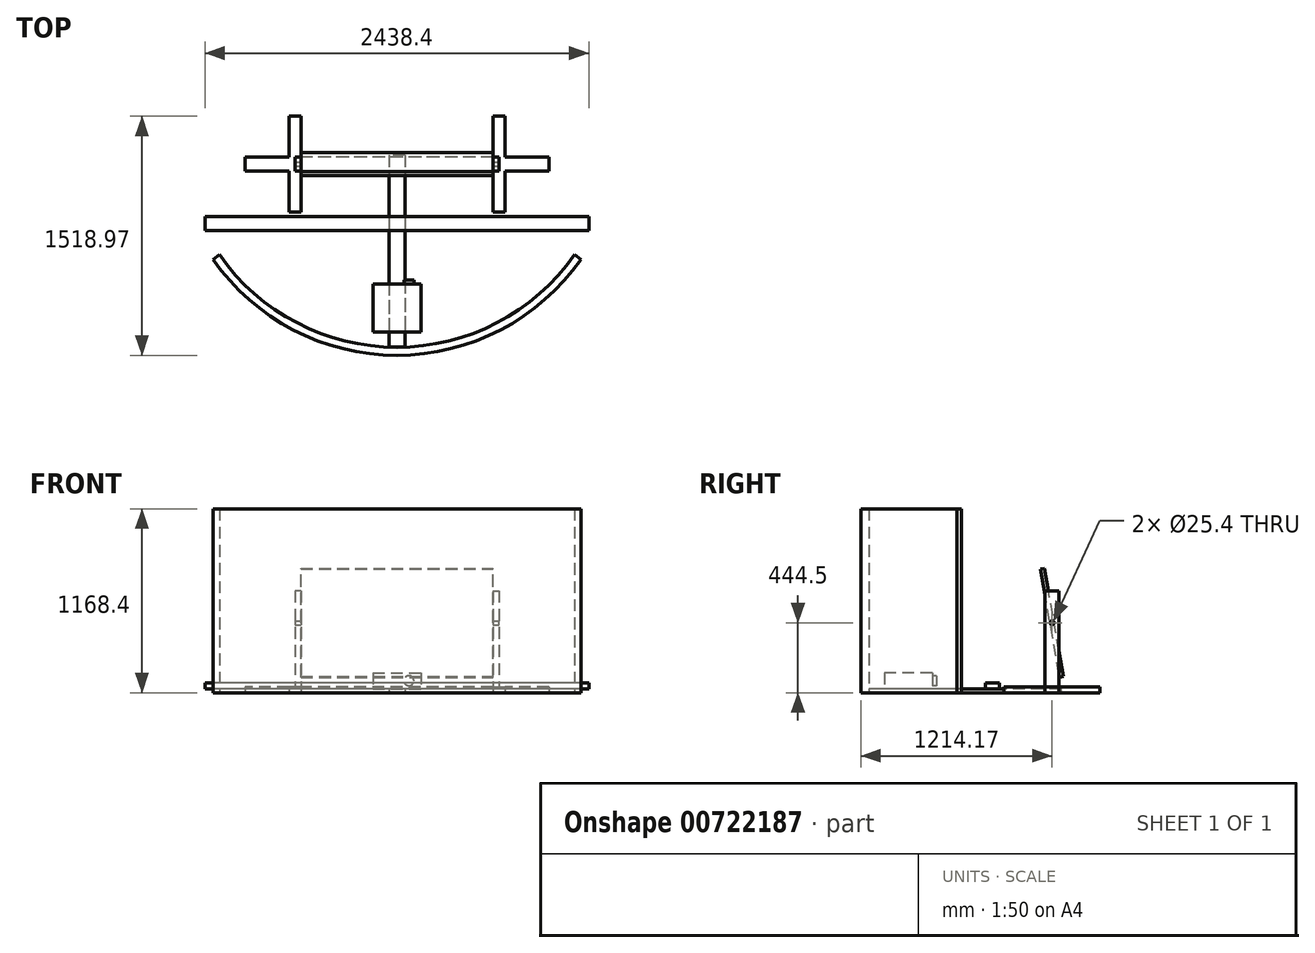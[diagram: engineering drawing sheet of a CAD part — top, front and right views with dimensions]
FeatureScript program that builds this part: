
annotation { "Feature Type Name" : "Feature", "Feature Type Description" : "" }
export const myFeature = defineFeature(function(context is Context, id is Id, definition is map)
    precondition{}
    {
        {
            var Q0;
            Q0=qCreatedBy(makeId("Top.planeOp"),FACE);
            var sketch = newSketch(context, id + "F0", { "sketchPlane" : qUnion([Q0])});
            skArc(sketch, "E0", {"start": v(-1168.4, -203.2) * mm, "mid": v(0, -812.8) * mm, "end": v(1168.4, -203.2) * mm});
            skLineSegment(sketch, "E1", {"start": v(0, 0) * mm, "end": v(0, -812.8) * mm, "construction": true});
            skPoint(sketch, "E2", {"position": v(0, -812.8) * mm});
            skArc(sketch, "E3.0", {"start": v(-1126.73, -174.14) * mm, "mid": v(0, -762) * mm, "end": v(1126.73, -174.14) * mm});
            skLineSegment(sketch, "E4", {"start": v(-1168.4, -203.2) * mm, "end": v(-1126.73, -174.14) * mm});
            skLineSegment(sketch, "E5", {"start": v(-1182.16, -183.48) * mm, "end": v(-1140.04, -243.86) * mm, "construction": true});
            skLineSegment(sketch, "E6.MirrorCS", {"start": v(1168.4, -203.2) * mm, "end": v(1126.73, -174.14) * mm});
            skSolve(sketch);
        }
        {
            var Q0;
            Q0 = qSketchRegion(id + "F0", true);
            extrude(context, id + "F1", {"entities" : qUnion([Q0]), "depth" : 1168.4 * mm, "offsetDistance" : 25.4 * mm});
        }
        {
            var Q0;
            Q0=qCreatedBy(makeId("Top.planeOp"),FACE);
            var sketch = newSketch(context, id + "F2", { "sketchPlane" : qUnion([Q0])});
            skLineSegment(sketch, "E7.bottom", {"start": v(50.8, 458.14) * mm, "end": v(-50.8, 458.14) * mm});
            skLineSegment(sketch, "E7.top", {"start": v(50.8, -761.06) * mm, "end": v(-50.8, -761.06) * mm});
            skLineSegment(sketch, "E7.left", {"start": v(50.8, 458.14) * mm, "end": v(50.8, -761.06) * mm});
            skLineSegment(sketch, "E7.right", {"start": v(-50.8, 458.14) * mm, "end": v(-50.8, -761.06) * mm});
            skPoint(sketch, "E7.middle", {"position": v(0, -151.46) * mm});
            skSolve(sketch);
        }
        {
            var Q0;
            Q0 = qSketchRegion(id + "F2", true);
            extrude(context, id + "F3", {"entities" : qUnion([Q0]), "depth" : 25.4 * mm, "offsetDistance" : 25.4 * mm});
        }
        {
            var Q0;
            Q0=makeQuery(id+"F3.opExtrude","CAP_FACE",FACE,{"disambiguationData":[OSD([sQuery(id+"F2.wireOp",EDGE,"E7.bottom"),sQuery(id+"F2.wireOp",EDGE,"E7.top"),sQuery(id+"F2.wireOp",EDGE,"E7.left"),sQuery(id+"F2.wireOp",EDGE,"E7.right")])],"isStart":false});
            var sketch = newSketch(context, id + "F4", { "sketchPlane" : qUnion([Q0])});
            skLineSegment(sketch, "E8.bottom", {"start": v(-152.4, -359.61) * mm, "end": v(152.4, -359.61) * mm});
            skLineSegment(sketch, "E8.top", {"start": v(-152.4, -664.41) * mm, "end": v(152.4, -664.41) * mm});
            skLineSegment(sketch, "E8.left", {"start": v(-152.4, -359.61) * mm, "end": v(-152.4, -664.41) * mm});
            skLineSegment(sketch, "E8.right", {"start": v(152.4, -359.61) * mm, "end": v(152.4, -664.41) * mm});
            skPoint(sketch, "E8.middle", {"position": v(0, -512.01) * mm});
            skSolve(sketch);
        }
        {
            var Q0;
            Q0 = qSketchRegion(id + "F4", true);
            extrude(context, id + "F5", {"entities" : qUnion([Q0]), "depth" : 101.6 * mm, "offsetDistance" : 25.4 * mm});
        }
        {
            var Q0;
            Q0=makeQuery(id+"F5.opExtrude","SWEPT_FACE",FACE,{"disambiguationData":[OSD([sQuery(id+"F4.wireOp",EDGE,"E8.bottom")])]});
            var sketch = newSketch(context, id + "F6", { "sketchPlane" : qUnion([Q0])});
            skCircle(sketch, "E9", {"center": v(-76.2, 76.2) * mm, "radius": 31.75 * mm});
            skLineSegment(sketch, "E10", {"start": v(-152.4, 76.2) * mm, "end": v(-13.38, 76.2) * mm, "construction": true});
            skSolve(sketch);
        }
        {
            var Q0;
            Q0 = qSketchRegion(id + "F6", true);
            extrude(context, id + "F7", {"entities" : qUnion([Q0]), "operationType" : NewBodyOperationType.ADD, "depth" : 25.4 * mm, "offsetDistance" : 25.4 * mm});
        }
        {
            var Q0;
            Q0=makeQuery(id+"F3.opExtrude","CAP_FACE",FACE,{"disambiguationData":[OSD([sQuery(id+"F2.wireOp",EDGE,"E7.bottom"),sQuery(id+"F2.wireOp",EDGE,"E7.top"),sQuery(id+"F2.wireOp",EDGE,"E7.left"),sQuery(id+"F2.wireOp",EDGE,"E7.right")])],"isStart":false});
            var sketch = newSketch(context, id + "F8", { "sketchPlane" : qUnion([Q0])});
            skLineSegment(sketch, "E11.bottom", {"start": v(1219.2, 67.16) * mm, "end": v(-1219.2, 67.16) * mm});
            skLineSegment(sketch, "E11.top", {"start": v(1219.2, -21.74) * mm, "end": v(-1219.2, -21.74) * mm});
            skLineSegment(sketch, "E11.left", {"start": v(1219.2, 67.16) * mm, "end": v(1219.2, -21.74) * mm});
            skLineSegment(sketch, "E11.right", {"start": v(-1219.2, 67.16) * mm, "end": v(-1219.2, -21.74) * mm});
            skPoint(sketch, "E11.middle", {"position": v(0, 22.71) * mm});
            skSolve(sketch);
        }
        {
            var Q0;
            Q0 = qSketchRegion(id + "F8", true);
            extrude(context, id + "F9", {"entities" : qUnion([Q0]), "depth" : 38.1 * mm, "offsetDistance" : 25.4 * mm});
        }
        {
            var Q0;
            Q0=qCreatedBy(makeId("Top.planeOp"),FACE);
            var sketch = newSketch(context, id + "F10", { "sketchPlane" : qUnion([Q0])});
            skLineSegment(sketch, "E12", {"start": v(0, -333.62) * mm, "end": v(0, 759.33) * mm, "construction": true});
            skLineSegment(sketch, "E13.bottom", {"start": v(609.6, 96.57) * mm, "end": v(685.8, 96.57) * mm});
            skLineSegment(sketch, "E13.top", {"start": v(609.6, 706.17) * mm, "end": v(685.8, 706.17) * mm});
            skLineSegment(sketch, "E13.left", {"start": v(609.6, 96.57) * mm, "end": v(609.6, 706.17) * mm});
            skLineSegment(sketch, "E13.right", {"start": v(685.8, 96.57) * mm, "end": v(685.8, 706.17) * mm});
            skLineSegment(sketch, "E14.MirrorCS", {"start": v(-609.6, 706.17) * mm, "end": v(-685.8, 706.17) * mm});
            skLineSegment(sketch, "E15.MirrorCS", {"start": v(-609.6, 96.57) * mm, "end": v(-685.8, 96.57) * mm});
            skLineSegment(sketch, "E16.MirrorCS", {"start": v(-685.8, 96.57) * mm, "end": v(-685.8, 706.17) * mm});
            skLineSegment(sketch, "E17.MirrorCS", {"start": v(-609.6, 96.57) * mm, "end": v(-609.6, 706.17) * mm});
            skLineSegment(sketch, "E18.bottom", {"start": v(965.2, 445.82) * mm, "end": v(-965.2, 445.82) * mm});
            skLineSegment(sketch, "E18.top", {"start": v(965.2, 356.92) * mm, "end": v(-965.2, 356.92) * mm});
            skLineSegment(sketch, "E18.left", {"start": v(965.2, 445.82) * mm, "end": v(965.2, 356.92) * mm});
            skLineSegment(sketch, "E18.right", {"start": v(-965.2, 445.82) * mm, "end": v(-965.2, 356.92) * mm});
            skPoint(sketch, "E18.middle", {"position": v(0, 401.37) * mm});
            skLineSegment(sketch, "E19", {"start": v(-965.2, 401.37) * mm, "end": v(-685.8, 401.37) * mm, "construction": true});
            skSolve(sketch);
        }
        {
            var Q0;
            Q0 = qSketchRegion(id + "F10", true);
            extrude(context, id + "F11", {"entities" : qUnion([Q0]), "depth" : 38.1 * mm, "offsetDistance" : 25.4 * mm});
        }
        {
            var Q0;
            Q0=makeQuery(id+"F11.opExtrude","CAP_FACE",FACE,{"disambiguationData":[OSD([sQuery(id+"F10.wireOp",EDGE,"E13.bottom"),sQuery(id+"F10.wireOp",EDGE,"E13.top"),sQuery(id+"F10.wireOp",EDGE,"E13.left"),sQuery(id+"F10.wireOp",EDGE,"E13.right"),sQuery(id+"F10.wireOp",EDGE,"E14.MirrorCS"),sQuery(id+"F10.wireOp",EDGE,"E15.MirrorCS"),sQuery(id+"F10.wireOp",EDGE,"E16.MirrorCS"),sQuery(id+"F10.wireOp",EDGE,"E17.MirrorCS"),sQuery(id+"F10.wireOp",EDGE,"E18.bottom"),sQuery(id+"F10.wireOp",EDGE,"E18.top"),sQuery(id+"F10.wireOp",EDGE,"E18.left"),sQuery(id+"F10.wireOp",EDGE,"E18.right")])],"isStart":false});
            var sketch = newSketch(context, id + "F12", { "sketchPlane" : qUnion([Q0])});
            skLineSegment(sketch, "E20", {"start": v(0, 192.88) * mm, "end": v(0, 698.3) * mm, "construction": true});
            skPoint(sketch, "E20.endSnap0", {"position": v(0, 445.82) * mm});
            skLineSegment(sketch, "E21.bottom", {"start": v(609.6, 356.92) * mm, "end": v(647.7, 356.92) * mm});
            skLineSegment(sketch, "E21.top", {"start": v(609.6, 445.82) * mm, "end": v(647.7, 445.82) * mm});
            skLineSegment(sketch, "E21.left", {"start": v(609.6, 356.92) * mm, "end": v(609.6, 445.82) * mm});
            skLineSegment(sketch, "E21.right", {"start": v(647.7, 356.92) * mm, "end": v(647.7, 445.82) * mm});
            skLineSegment(sketch, "E22.MirrorCS", {"start": v(-647.7, 356.92) * mm, "end": v(-647.7, 445.82) * mm});
            skLineSegment(sketch, "E23.MirrorCS", {"start": v(-609.6, 356.92) * mm, "end": v(-609.6, 445.82) * mm});
            skLineSegment(sketch, "E24.MirrorCS", {"start": v(-609.6, 445.82) * mm, "end": v(-647.7, 445.82) * mm});
            skLineSegment(sketch, "E25.MirrorCS", {"start": v(-609.6, 356.92) * mm, "end": v(-647.7, 356.92) * mm});
            skSolve(sketch);
        }
        {
            var Q0;
            Q0 = qSketchRegion(id + "F12", true);
            extrude(context, id + "F13", {"entities" : qUnion([Q0]), "operationType" : NewBodyOperationType.ADD, "depth" : 609.6 * mm, "offsetDistance" : 25.4 * mm});
        }
        {
            var Q0;
            Q0=makeQuery(id+"F13.opExtrude","SWEPT_FACE",FACE,{"disambiguationData":[OSD([sQuery(id+"F12.wireOp",EDGE,"E21.right")])]});
            var sketch = newSketch(context, id + "F14", { "sketchPlane" : qUnion([Q0])});
            skCircle(sketch, "E26", {"center": v(401.37, 444.5) * mm, "radius": 12.7 * mm});
            skLineSegment(sketch, "E27", {"start": v(401.37, 647.7) * mm, "end": v(401.37, 38.1) * mm, "construction": true});
            skSolve(sketch);
        }
        {
            var Q0;
            Q0 = qSketchRegion(id + "F14", true);
            extrude(context, id + "F15", {"entities" : qUnion([Q0]), "operationType" : NewBodyOperationType.REMOVE, "endBound" : BoundingType.THROUGH_ALL, "oppositeDirection" : true, "depth" : 25.4 * mm, "offsetDistance" : 25.4 * mm});
        }
        {
            var Q0;
            Q0=makeQuery(id+"F13.opExtrude","SWEPT_FACE",FACE,{"disambiguationData":[OSD([sQuery(id+"F12.wireOp",EDGE,"E24.MirrorCS")])]});
            cPlane(context, id + "F16", {"entities" : qUnion([Q0]), "cplaneType" : CPlaneType.OFFSET, "offset" : 44.45 * mm, "oppositeDirection" : true, "width" : 152.4 * mm, "height" : 152.4 * mm});
        }
        {
            var Q0;
            Q0=qCreatedBy(id+"F16.planeOp",FACE);
            var sketch = newSketch(context, id + "F17", { "sketchPlane" : qUnion([Q0])});
            skLineSegment(sketch, "E28", {"start": v(-816.37, 444.5) * mm, "end": v(763.07, 444.5) * mm, "construction": true});
            skSolve(sketch);
        }
        {
            var Q0;
            Q0=sQuery(id+"F17.wireOp",EDGE,"E28");
            cPlane(context, id + "F18", {"entities" : qUnion([Q0]), "cplaneType" : CPlaneType.LINE_ANGLE, "offset" : 25.4 * mm, "angle" : 10 * degree, "oppositeDirection" : true, "width" : 152.4 * mm, "height" : 152.4 * mm});
        }
        {
            var Q0;
            Q0=qCreatedBy(id+"F18.planeOp",FACE);
            var sketch = newSketch(context, id + "F19", { "sketchPlane" : qUnion([Q0])});
            skLineSegment(sketch, "E29.bottom", {"start": v(-609.6, 18.8) * mm, "end": v(609.6, 18.8) * mm});
            skLineSegment(sketch, "E29.top", {"start": v(-609.6, 717.3) * mm, "end": v(609.6, 717.3) * mm});
            skLineSegment(sketch, "E29.left", {"start": v(-609.6, 18.8) * mm, "end": v(-609.6, 717.3) * mm});
            skLineSegment(sketch, "E29.right", {"start": v(609.6, 18.8) * mm, "end": v(609.6, 717.3) * mm});
            skPoint(sketch, "E29.middle", {"position": v(0, 368.05) * mm});
            skSolve(sketch);
        }
        {
            var Q0;
            Q0 = qSketchRegion(id + "F19", true);
            extrude(context, id + "F20", {"entities" : qUnion([Q0]), "endBound" : BoundingType.SYMMETRIC, "depth" : 25.4 * mm, "offsetDistance" : 25.4 * mm});
        }
    });
